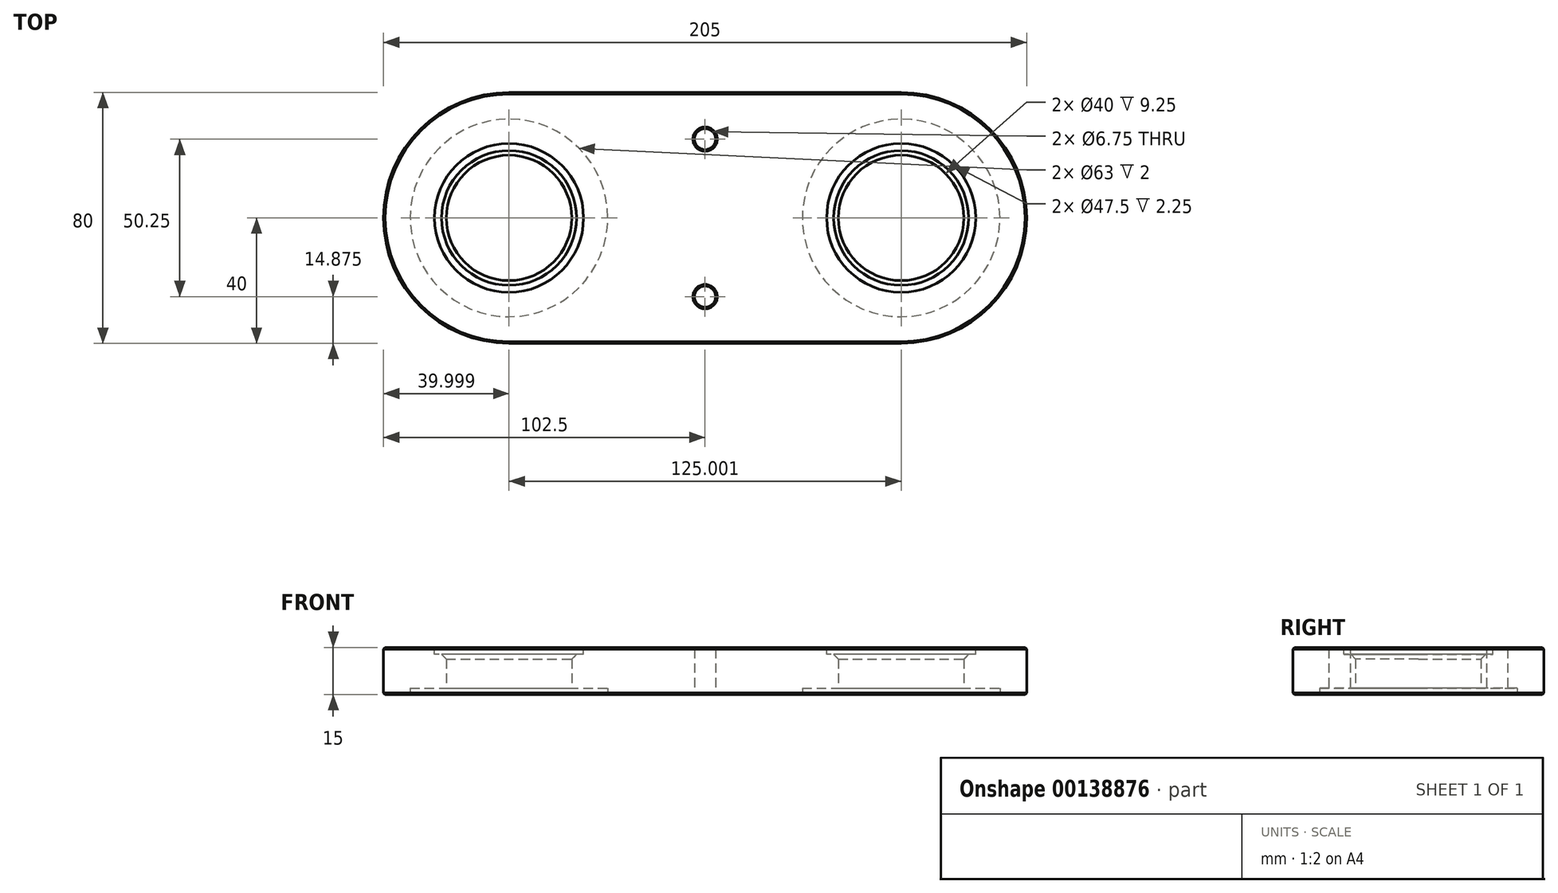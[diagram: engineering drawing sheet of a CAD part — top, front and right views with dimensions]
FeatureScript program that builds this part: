
annotation { "Feature Type Name" : "Feature", "Feature Type Description" : "" }
export const myFeature = defineFeature(function(context is Context, id is Id, definition is map)
    precondition{}
    {
        {
            var Q0;
            Q0=qCreatedBy(makeId("Top.planeOp"),FACE);
            var sketch = newSketch(context, id + "F0", { "sketchPlane" : qUnion([Q0])});
            skLineSegment(sketch, "E0.bottom", {"start": v(-62.5, -40) * mm, "end": v(62.5, -40) * mm});
            skLineSegment(sketch, "E0.top", {"start": v(-62.5, 40) * mm, "end": v(62.5, 40) * mm});
            skLineSegment(sketch, "E0.left", {"start": v(-102.5, -0.23) * mm, "end": v(-102.5, 0.23) * mm});
            skLineSegment(sketch, "E0.right", {"start": v(102.5, -0.23) * mm, "end": v(102.5, 0.23) * mm});
            skPoint(sketch, "E0.middle", {"position": v(0, 0) * mm});
            skArc(sketch, "E1", {"start": v(-62.5, 40) * mm, "mid": v(-102.5, 0) * mm, "end": v(-62.5, -40) * mm});
            skPoint(sketch, "E1.first.point", {"position": v(-102.5, 0) * mm});
            skPoint(sketch, "E1.second.point", {"position": v(-22.5, 0) * mm});
            skPoint(sketch, "E1.second.point.positionSnap0", {"position": v(-102.5, 0) * mm});
            skCircle(sketch, "E2", {"center": v(-62.5, 0) * mm, "radius": 20 * mm});
            skPoint(sketch, "E3.orphan", {"position": v(-102.5, -40) * mm});
            skPoint(sketch, "E4.orphan", {"position": v(-102.5, 40) * mm});
            skCircle(sketch, "E5.MirrorC", {"center": v(62.5, 0) * mm, "radius": 20 * mm});
            skArc(sketch, "E6.MirrorCS", {"start": v(62.5, 40) * mm, "mid": v(102.5, 0) * mm, "end": v(62.5, -40) * mm});
            skPoint(sketch, "E7.orphan", {"position": v(102.5, -40) * mm});
            skPoint(sketch, "E8.orphan", {"position": v(102.5, 40) * mm});
            skCircle(sketch, "E9", {"center": v(0, 25.13) * mm, "radius": 3.38 * mm});
            skCircle(sketch, "E10.MirrorC", {"center": v(0, -25.13) * mm, "radius": 3.38 * mm});
            skSolve(sketch);
        }
        {
            var Q0;
            Q0 = qSketchRegion(id + "F0", true);
            extrude(context, id + "F1", {"entities" : qUnion([Q0]), "depth" : 15 * mm});
        }
        {
            var Q0;
            Q0=makeQuery(id+"F1.opExtrude","CAP_FACE",FACE,{"disambiguationData":[OSD([sQuery(id+"F0.wireOp",EDGE,"E0.bottom"),sQuery(id+"F0.wireOp",EDGE,"E0.top"),sQuery(id+"F0.wireOp",EDGE,"E1"),sQuery(id+"F0.wireOp",EDGE,"E2"),sQuery(id+"F0.wireOp",EDGE,"E5.MirrorC"),sQuery(id+"F0.wireOp",EDGE,"E6.MirrorCS")])],"isStart":true});
            var sketch = newSketch(context, id + "F2", { "sketchPlane" : qUnion([Q0])});
            skCircle(sketch, "E11", {"center": v(-62.5, 0) * mm, "radius": 31.5 * mm});
            skCircle(sketch, "E12.MirrorC", {"center": v(62.5, 0) * mm, "radius": 31.5 * mm});
            skSolve(sketch);
        }
        {
            var Q0;
            Q0 = qSketchRegion(id + "F2", true);
            extrude(context, id + "F3", {"entities" : qUnion([Q0]), "operationType" : NewBodyOperationType.REMOVE, "oppositeDirection" : true, "depth" : 2 * mm});
        }
        {
            var Q0;
            Q0=makeQuery(id+"F1.opExtrude","SWEPT_FACE",FACE,{"disambiguationData":[OSD([sQuery(id+"F0.wireOp",EDGE,"E0.top")])]});
            chamfer(context, id + "F4", {"entities" : qUnion([Q0]), "width" : .5 * mm, "tangentPropagation" : true});
        }
        {
            var Q0;
            Q0=makeQuery(id+"F1.opExtrude","CAP_EDGE",EDGE,{"disambiguationData":[OSD([sQuery(id+"F0.wireOp",EDGE,"E10.MirrorC")])],"isStart":false});
            var Q1;
            Q1=makeQuery(id+"F1.opExtrude","CAP_EDGE",EDGE,{"disambiguationData":[OSD([sQuery(id+"F0.wireOp",EDGE,"E9")])],"isStart":false});
            var Q2;
            Q2=makeQuery(id+"F1.opExtrude","CAP_EDGE",EDGE,{"disambiguationData":[OSD([sQuery(id+"F0.wireOp",EDGE,"E10.MirrorC")])],"isStart":true});
            var Q3;
            Q3=makeQuery(id+"F1.opExtrude","CAP_EDGE",EDGE,{"disambiguationData":[OSD([sQuery(id+"F0.wireOp",EDGE,"E9")])],"isStart":true});
            chamfer(context, id + "F5", {"entities" : qUnion([Q0, Q1, Q2, Q3]), "width" : .5 * mm, "tangentPropagation" : true});
        }
        {
            var Q0;
            Q0=makeQuery(id+"F1.opExtrude","CAP_FACE",FACE,{"disambiguationData":[OSD([sQuery(id+"F0.wireOp",EDGE,"E0.bottom"),sQuery(id+"F0.wireOp",EDGE,"E0.top"),sQuery(id+"F0.wireOp",EDGE,"E1"),sQuery(id+"F0.wireOp",EDGE,"E2"),sQuery(id+"F0.wireOp",EDGE,"E5.MirrorC"),sQuery(id+"F0.wireOp",EDGE,"E6.MirrorCS"),sQuery(id+"F0.wireOp",EDGE,"E9"),sQuery(id+"F0.wireOp",EDGE,"E10.MirrorC")])],"isStart":false});
            var sketch = newSketch(context, id + "F6", { "sketchPlane" : qUnion([Q0])});
            skCircle(sketch, "E13", {"center": v(-62.5, 0) * mm, "radius": 23.75 * mm});
            skCircle(sketch, "E14.MirrorC", {"center": v(62.5, 0) * mm, "radius": 23.75 * mm});
            skSolve(sketch);
        }
        {
            var Q0;
            Q0 = qSketchRegion(id + "F6", true);
            extrude(context, id + "F7", {"entities" : qUnion([Q0]), "operationType" : NewBodyOperationType.REMOVE, "oppositeDirection" : true, "depth" : 2.25 * mm});
        }
        {
            var Q0;
            Q0=makeQuery(id+"F7.boolean.opBoolean","INTERSECT",EDGE,{"derivedFrom":[makeQuery(id+"F1.opExtrude","SWEPT_FACE",FACE,{"disambiguationData":[OSD([sQuery(id+"F0.wireOp",EDGE,"E2")])]}),makeQuery(id+"F7.opExtrude","CAP_FACE",FACE,{"disambiguationData":[OSD([sQuery(id+"F6.wireOp",EDGE,"E13")])],"isStart":false})]});
            var Q1;
            Q1=makeQuery(id+"F7.boolean.opBoolean","INTERSECT",EDGE,{"derivedFrom":[makeQuery(id+"F1.opExtrude","SWEPT_FACE",FACE,{"disambiguationData":[OSD([sQuery(id+"F0.wireOp",EDGE,"E5.MirrorC")])]}),makeQuery(id+"F7.opExtrude","CAP_FACE",FACE,{"disambiguationData":[OSD([sQuery(id+"F6.wireOp",EDGE,"E14.MirrorC")])],"isStart":false})]});
            chamfer(context, id + "F8", {"entities" : qUnion([Q0, Q1]), "width" : 1.5 * mm, "tangentPropagation" : true});
        }
    });
